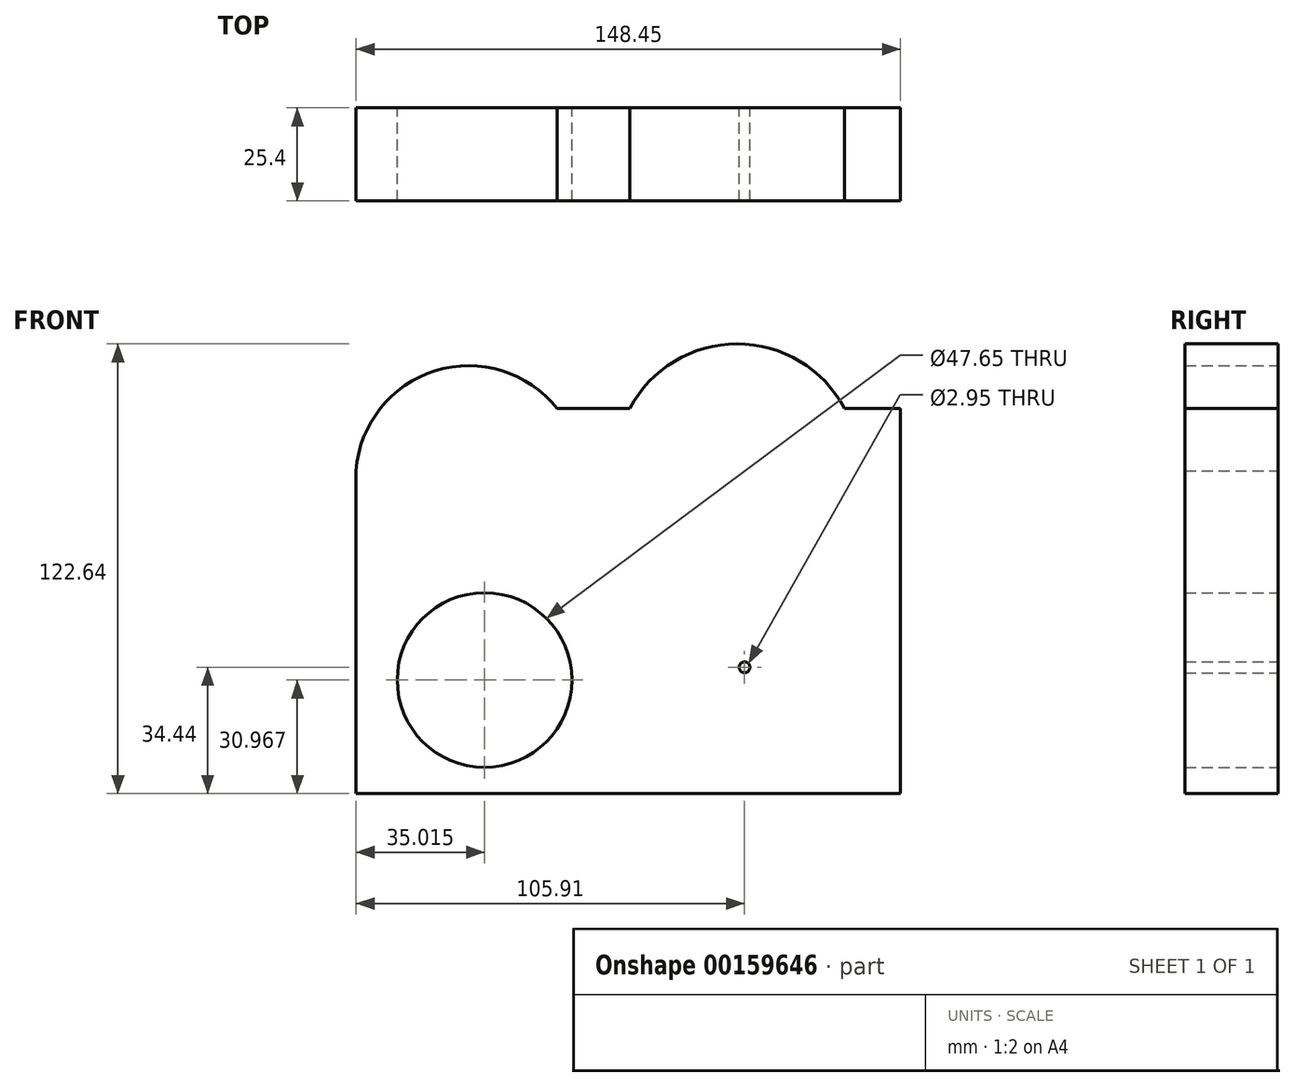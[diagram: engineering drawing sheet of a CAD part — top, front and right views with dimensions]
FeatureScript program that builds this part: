
annotation { "Feature Type Name" : "Feature", "Feature Type Description" : "" }
export const myFeature = defineFeature(function(context is Context, id is Id, definition is map)
    precondition{}
    {
        {
            var Q0;
            Q0=qCreatedBy(makeId("Front.planeOp"),FACE);
            var sketch = newSketch(context, id + "F0", { "sketchPlane" : qUnion([Q0])});
            skLineSegment(sketch, "E0.bottom", {"start": v(-73.79, 54.84) * mm, "end": v(74.66, 54.84) * mm});
            skLineSegment(sketch, "E0.top", {"start": v(-73.79, -50.2) * mm, "end": v(74.66, -50.2) * mm});
            skLineSegment(sketch, "E0.left", {"start": v(-73.79, 54.84) * mm, "end": v(-73.79, -50.2) * mm});
            skLineSegment(sketch, "E0.right", {"start": v(74.66, 54.84) * mm, "end": v(74.66, -50.2) * mm});
            skCircle(sketch, "E1", {"center": v(-43.12, 35.74) * mm, "radius": 30.75 * mm});
            skCircle(sketch, "E2", {"center": v(30.1, 39.2) * mm, "radius": 33.22 * mm});
            skCircle(sketch, "E3", {"center": v(32.12, -15.77) * mm, "radius": 1.48 * mm});
            skCircle(sketch, "E4", {"center": v(32.12, -15.77) * mm, "radius": 1.45 * mm});
            skCircle(sketch, "E5", {"center": v(32.12, -15.77) * mm, "radius": 16.18 * mm});
            skCircle(sketch, "E6", {"center": v(-38.78, -19.24) * mm, "radius": 23.82 * mm});
            skSolve(sketch);
        }
        {
            var Q0;
            {var subQ0=sQuery(id+"F0.wireOp",EDGE,"E2");var subQ1=sQuery(id+"F0.wireOp",EDGE,"E0.bottom");var subQ2=makeQuery(id+"F0.imprint","INTERSECT",VERTEX,{"disambiguationData":[OD(0.0)],"derivedFrom":[subQ1,subQ0]});Q0=makeQuery(id+"F0.imprint","IMPRINT",FACE,{"disambiguationData":[TD([[makeQuery(id+"F0.imprint","IMPRINT",EDGE,{"disambiguationData":[TD([[subQ2,-1.0]])],"derivedFrom":subQ1}),1.0]])]});}
            var Q1;
            {var subQ0=sQuery(id+"F0.wireOp",EDGE,"E2");var subQ1=sQuery(id+"F0.wireOp",EDGE,"E0.bottom");var subQ2=makeQuery(id+"F0.imprint","INTERSECT",VERTEX,{"disambiguationData":[OD(0.0)],"derivedFrom":[subQ1,subQ0]});Q1=makeQuery(id+"F0.imprint","IMPRINT",FACE,{"disambiguationData":[TD([[makeQuery(id+"F0.imprint","IMPRINT",EDGE,{"disambiguationData":[TD([[subQ2,-1.0]])],"derivedFrom":subQ1}),-1.0]])]});}
            var Q2;
            {var subQ0=sQuery(id+"F0.wireOp",EDGE,"E1");var subQ1=sQuery(id+"F0.wireOp",EDGE,"E0.bottom");var subQ2=makeQuery(id+"F0.imprint","INTERSECT",VERTEX,{"disambiguationData":[OD(0.0)],"derivedFrom":[subQ1,subQ0]});Q2=makeQuery(id+"F0.imprint","IMPRINT",FACE,{"disambiguationData":[TD([[makeQuery(id+"F0.imprint","IMPRINT",EDGE,{"disambiguationData":[TD([[subQ2,-1.0]])],"derivedFrom":subQ1}),-1.0]])]});}
            var Q3;
            {var subQ0=sQuery(id+"F0.wireOp",EDGE,"E1");var subQ1=sQuery(id+"F0.wireOp",EDGE,"E0.bottom");var subQ2=makeQuery(id+"F0.imprint","INTERSECT",VERTEX,{"disambiguationData":[OD(0.0)],"derivedFrom":[subQ1,subQ0]});Q3=makeQuery(id+"F0.imprint","IMPRINT",FACE,{"disambiguationData":[TD([[makeQuery(id+"F0.imprint","IMPRINT",EDGE,{"disambiguationData":[TD([[subQ2,-1.0]])],"derivedFrom":subQ1}),1.0]])]});}
            var Q4;
            {var subQ1=sQuery(id+"F0.wireOp",EDGE,"E0.top");Q4=makeQuery(id+"F0.imprint","IMPRINT",FACE,{"disambiguationData":[TD([[makeQuery(id+"F0.imprint","IMPRINT",EDGE,{"derivedFrom":subQ1}),1.0]])]});}
            var Q5;
            Q5=makeQuery(id+"F0.imprint","IMPRINT",FACE,{"disambiguationData":[TD([[makeQuery(id+"F0.imprint","IMPRINT",EDGE,{"derivedFrom":sQuery(id+"F0.wireOp",EDGE,"E3")}),-1.0]])]});
            var Q6;
            Q6=sQuery(id+"F0.wireOp",EDGE,"E1");
            extrude(context, id + "F1", {"entities" : qUnion([Q0, Q1, Q2, Q3, Q4, Q5]), "surfaceEntities" : qUnion([Q6]), "depth" : 25.4 * mm});
        }
    });
